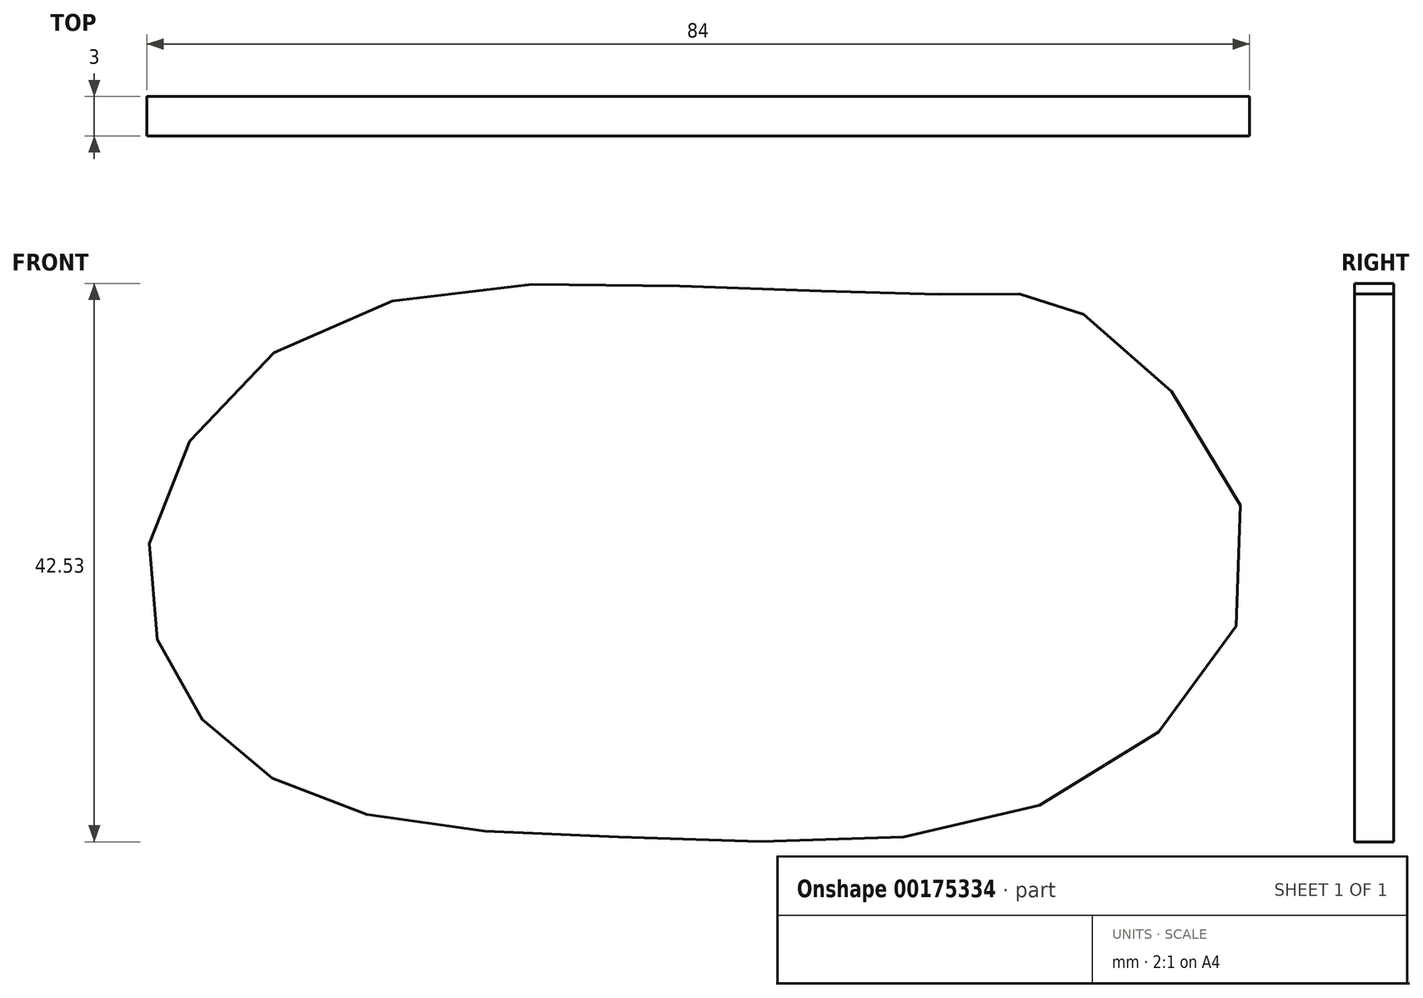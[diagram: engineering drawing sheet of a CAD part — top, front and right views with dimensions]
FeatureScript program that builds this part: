
annotation { "Feature Type Name" : "Feature", "Feature Type Description" : "" }
export const myFeature = defineFeature(function(context is Context, id is Id, definition is map)
    precondition{}
    {
        {
            var Q0;
            Q0=qCreatedBy(makeId("Front.planeOp"),FACE);
            var sketch = newSketch(context, id + "F0", { "sketchPlane" : qUnion([Q0])});
            skPoint(sketch, "E0.0.internal.orphan", {"position": v(-64.04, 0) * mm});
            skPoint(sketch, "E0.3.internal.orphan", {"position": v(57.42, 0) * mm});
            skFitSpline(sketch, "E1", {"points": [v(-64.04, 0) * mm, v(-51.95, 16.12) * mm, v(-22.02, 19.57) * mm, v(0, 19) * mm, v(6.48, 17.84) * mm, v(19.71, 0) * mm, v(5.32, -19.28) * mm, v(-24.9, -22.45) * mm, v(-49.36, -20.15) * mm, v(-60.58, -12.66) * mm, v(-64.04, 0) * mm]});
            skSolve(sketch);
        }
        {
            var Q0;
            Q0=makeQuery(id+"F0.imprint","IMPRINT",FACE,{"disambiguationData":[TD([[makeQuery(id+"F0.imprint","IMPRINT",EDGE,{"derivedFrom":sQuery(id+"F0.wireOp",EDGE,"E1")}),-1.0]])]});
            extrude(context, id + "F1", {"entities" : qUnion([Q0]), "depth" : 3 * mm});
        }
    });
